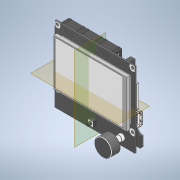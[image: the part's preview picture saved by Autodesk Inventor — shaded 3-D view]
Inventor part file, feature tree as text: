
AUTODESK INVENTOR PART (.ipt)
format: ipt  version: 2022 (Build 260153000, 153)  size: 5,241,344 bytes
history: native  units: in
note: dims shown in document units (in); Inventor stores cm internally (conversion verified against a paired STEP export)
features: other x55, plane x2
ambient origin geometry x8: Origin, YZ Plane, XZ Plane, XY Plane, X Axis, Y Axis, Z Axis, Center Point
bodies: Solid1 (feature_tree), Solid2 (feature_tree), Solid3 (feature_tree), Solid4 (feature_tree), Solid5 (feature_tree), Solid6 (feature_tree), Solid7 (feature_tree), Solid8 (feature_tree), Solid9 (feature_tree), Solid10 (feature_tree), Solid11 (feature_tree), Solid12 (feature_tree), Solid13 (feature_tree), Solid14 (feature_tree), Solid15 (feature_tree), Solid16 (feature_tree), Solid17 (feature_tree), Solid18 (feature_tree), Solid19 (feature_tree), Solid20 (feature_tree), Solid21 (feature_tree), Solid22 (feature_tree), Solid23 (feature_tree), Solid24 (feature_tree), Solid25 (feature_tree), Solid26 (feature_tree), Solid27 (feature_tree), Solid28 (feature_tree), Solid29 (feature_tree), Solid30 (feature_tree), Solid31 (feature_tree), Solid32 (feature_tree), Solid33 (feature_tree), Solid34 (feature_tree), Solid35 (feature_tree), Solid36 (feature_tree), Solid37 (feature_tree), Solid38 (feature_tree), Solid39 (feature_tree), Solid40 (feature_tree), Solid41 (feature_tree), Solid42 (feature_tree), Solid43 (feature_tree), Solid44 (feature_tree), Solid45 (feature_tree), Solid46 (feature_tree), Solid47 (feature_tree), Solid48 (feature_tree), Solid49 (feature_tree), Solid50 (feature_tree), Solid51 (feature_tree), Solid52 (feature_tree), Solid53 (feature_tree), Solid54 (feature_tree), Solid55 (feature_tree), Solid56 (feature_tree)
feature tree (57):
  plane  "Work Plane1"
  plane  "Work Plane2"
  other  "PCB_1:1"
  other  "Reset_1_Reset_Corpo1_1:1"
  other  "cap_1_cap_Corpo1_1:1"
  other  "TFT Display_1:1"
  other  "Straight Contact_13_Straight Contact_Corpo1_1:1"
  other  "Straight Contact_6_Straight Contact_Corpo1_1:1"
  other  "Straight Contact_5_Straight Contact_Corpo1_1:1"
  other  "Straight Contact_12_Straight Contact_Corpo1_1:1"
  other  "Straight Contact_11_Straight Contact_Corpo1_1:1"
  other  "Straight Contact_4_Straight Contact_Corpo1_1:1"
  other  "Straight Contact_3_Straight Contact_Corpo1_1:1"
  other  "Straight Contact_10_Straight Contact_Corpo1_1:1"
  other  "Straight Contact_9_Straight Contact_Corpo1_1:1"
  other  "Straight Contact_2_Straight Contact_Corpo1_1:1"
  other  "14_Pin Shrouded Header Body_1_14_Pin Shrouded Header Body_Corpo1_1:1"
  other  "Straight Contact_13_Straight Contact_Corpo1 (1)_1:1"
  other  "Straight Contact_6_Straight Contact_Corpo1 (1)_1:1"
  other  "Straight Contact_5_Straight Contact_Corpo1 (1)_1:1"
  other  "Straight Contact_12_Straight Contact_Corpo1 (1)_1:1"
  other  "Straight Contact_11_Straight Contact_Corpo1 (1)_1:1"
  other  "Straight Contact_4_Straight Contact_Corpo1 (1)_1:1"
  other  "Straight Contact_3_Straight Contact_Corpo1 (1)_1:1"
  other  "Straight Contact_10_Straight Contact_Corpo1 (1)_1:1"
  other  "Straight Contact_9_Straight Contact_Corpo1 (1)_1:1"
  other  "Straight Contact_2_Straight Contact_Corpo1 (1)_1:1"
  other  "14_Pin Shrouded Header Body_1_14_Pin Shrouded Header Body_Corpo1 (1)_1:1"
  other  "Straight Contact_13_Straight Contact_Corpo1 (2)_1:1"
  other  "Straight Contact_6_Straight Contact_Corpo1 (2)_1:1"
  other  "Straight Contact_5_Straight Contact_Corpo1 (2)_1:1"
  other  "Straight Contact_12_Straight Contact_Corpo1 (2)_1:1"
  other  "Straight Contact_11_Straight Contact_Corpo1 (2)_1:1"
  other  "Straight Contact_4_Straight Contact_Corpo1 (2)_1:1"
  other  "Straight Contact_3_Straight Contact_Corpo1 (2)_1:1"
  other  "Straight Contact_10_Straight Contact_Corpo1 (2)_1:1"
  other  "Straight Contact_9_Straight Contact_Corpo1 (2)_1:1"
  other  "Straight Contact_2_Straight Contact_Corpo1 (2)_1:1"
  other  "14_Pin Shrouded Header Body_1_14_Pin Shrouded Header Body_Corpo1 (2)_1:1"
  other  "JST _ XH _ SMD _R_ _ 5Pin _ 2_54mm v1_2_JST _ XH _ SMD _R_ _ 5Pin _ 2_54mm_Corpo1_1:1"
  other  "JST _ XH _ SMD _R_ _ 5Pin _ 2_54mm v1_2_JST _ XH _ SMD _R_ _ 5Pin _ 2_54mm_Corpo1 (1)_1:1"
  other  "JST _ XH _ SMD _R_ _ 2Pin _ 2_54mm v2_1_JST _ XH _ SMD _R_ _ 2Pin _ 2_54mm_Corpo1_1:1"
  other  "JST _ XH _ SMD _R_ _ 3Pin _ 2_54mm v1_4_JST _ XH _ SMD _R_ _ 3Pin _ 2_54mm_Corpo1_1:1"
  other  "JST _ XH _ SMD _R_ _ 3Pin _ 2_54mm v1_4_JST _ XH _ SMD _R_ _ 3Pin _ 2_54mm_Corpo1 (1)_1:1"
  other  "JST _ XH _ SMD _R_ _ 3Pin _ 2_54mm v1_4_JST _ XH _ SMD _R_ _ 3Pin _ 2_54mm_Corpo1 (2)_1:1"
  other  "JST _ XH _ SMD _R_ _ 3Pin _ 2_54mm v1_4_JST _ XH _ SMD _R_ _ 3Pin _ 2_54mm_Corpo1 (3)_1:1"
  other  "Buzzer_1_Buzzer_Corpo1_1:1"
  other  "PBD_8 v3_1_PBD_8_Corpo1_1:1"
  other  "SD Slot_1_SD Slot_Corpo1_1:1"
  other  "Componente4_1_Componente4_Corpo1_1:1"
  other  "Componente3_1_Componente3_Corpo1_1:1"
  other  "Componente6_1_Componente6_Corpo1_1:1"
  other  "Componente7_1_Componente7_Corpo1_1:1"
  other  "Componente2_1_Componente2_Corpo1_1:1"
  other  "Componente8_1_Componente8_Corpo1_1:1"
  other  "Componente5_1_Componente5_Corpo1_1:1"
  other  "Componente9_1_Componente9_Corpo1_1:1"
